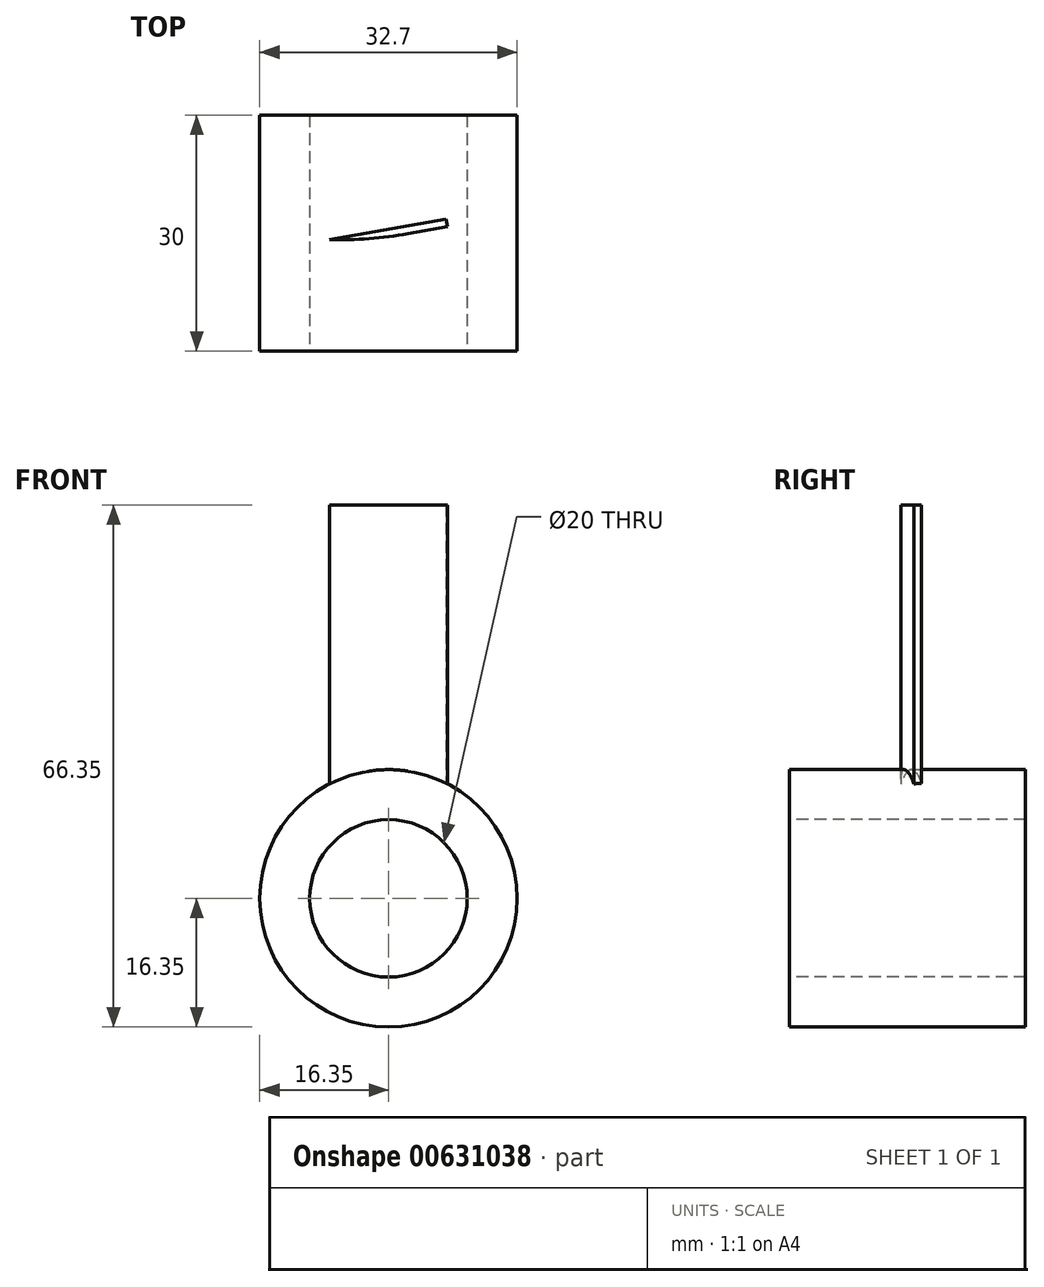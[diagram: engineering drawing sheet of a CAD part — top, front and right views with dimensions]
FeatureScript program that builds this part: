
annotation { "Feature Type Name" : "Feature", "Feature Type Description" : "" }
export const myFeature = defineFeature(function(context is Context, id is Id, definition is map)
    precondition{}
    {
        {
            var Q0;
            Q0=qCreatedBy(makeId("Front.planeOp"),FACE);
            var sketch = newSketch(context, id + "F0", { "sketchPlane" : qUnion([Q0])});
            skCircle(sketch, "E0", {"center": v(0, 0) * mm, "radius": 16.35 * mm});
            skSolve(sketch);
        }
        {
            var Q0;
            Q0 = qSketchRegion(id + "F0", true);
            extrude(context, id + "F1", {"entities" : qUnion([Q0]), "endBound" : BoundingType.SYMMETRIC, "depth" : 30 * mm, "offsetDistance" : 25.4 * mm});
        }
        {
            var Q0;
            Q0=qCreatedBy(makeId("Top.planeOp"),FACE);
            cPlane(context, id + "F2", {"entities" : qUnion([Q0]), "cplaneType" : CPlaneType.OFFSET, "offset" : 10 * mm, "width" : 150 * mm, "height" : 150 * mm});
        }
        {
            var Q0;
            Q0=qCreatedBy(id+"F2.planeOp",FACE);
            var sketch = newSketch(context, id + "F3", { "sketchPlane" : qUnion([Q0])});
            skLineSegment(sketch, "E1.bottom", {"start": v(7.47, 0.8) * mm, "end": v(-7.3, -1.8) * mm});
            skLineSegment(sketch, "E1.top", {"start": v(7.3, 1.8) * mm, "end": v(-7.47, -0.8) * mm});
            skLineSegment(sketch, "E1.left", {"start": v(7.47, 0.8) * mm, "end": v(7.39, 1.3) * mm});
            skLineSegment(sketch, "E1.right", {"start": v(-7.3, -1.8) * mm, "end": v(-7.39, -1.3) * mm});
            skPoint(sketch, "E1.middle", {"position": v(0, 0) * mm});
            skLineSegment(sketch, "E2", {"start": v(-7.39, -1.3) * mm, "end": v(-7.47, -0.8) * mm});
            skLineSegment(sketch, "E3", {"start": v(7.39, 1.3) * mm, "end": v(7.3, 1.8) * mm});
            skLineSegment(sketch, "E4", {"start": v(-7.39, -1.3) * mm, "end": v(0, 0) * mm});
            skLineSegment(sketch, "E5", {"start": v(0, 0) * mm, "end": v(7.39, 1.3) * mm});
            skSolve(sketch);
        }
        {
            var Q0;
            Q0 = qSketchRegion(id + "F3", true);
            extrude(context, id + "F4", {"entities" : qUnion([Q0]), "operationType" : NewBodyOperationType.ADD, "depth" : 40 * mm, "offsetDistance" : 25 * mm});
        }
        {
            var Q0;
            Q0=qCreatedBy(makeId("Top.planeOp"),FACE);
            var sketch = newSketch(context, id + "F5", { "sketchPlane" : qUnion([Q0])});
            skLineSegment(sketch, "E6", {"start": v(0, 34.93) * mm, "end": v(0, -35.3) * mm});
            skSolve(sketch);
        }
        {
            var Q0;
            Q0=makeQuery(id+"F1.opExtrude","CAP_FACE",FACE,{"disambiguationData":[OSD([sQuery(id+"F0.wireOp",EDGE,"E0")])],"isStart":false});
            var sketch = newSketch(context, id + "F6", { "sketchPlane" : qUnion([Q0])});
            skCircle(sketch, "E7", {"center": v(0, 0) * mm, "radius": 10 * mm});
            skSolve(sketch);
        }
        {
            var Q0;
            Q0 = qSketchRegion(id + "F6", true);
            extrude(context, id + "F7", {"entities" : qUnion([Q0]), "operationType" : NewBodyOperationType.REMOVE, "endBound" : BoundingType.THROUGH_ALL, "oppositeDirection" : true, "depth" : 25 * mm, "offsetDistance" : 25 * mm});
        }
        {
            var Q0;
            Q0=makeQuery(id+"F4.opExtrude","SWEPT_EDGE",EDGE,{"disambiguationData":[OSD([sQuery(id+"F3.wireOp",EDGE,"E1.bottom"),sQuery(id+"F3.wireOp",EDGE,"E1.right")])]});
            var Q1;
            Q1=makeQuery(id+"FS7XTIEs3ckikAF_1.1.F4.opExtrude","SWEPT_EDGE",EDGE,{"disambiguationData":[OSD([sQuery(id+"F3.wireOp",EDGE,"E1.bottom"),sQuery(id+"F3.wireOp",EDGE,"E1.right")])]});
            var Q2;
            Q2=makeQuery(id+"FS7XTIEs3ckikAF_1.2.F4.opExtrude","SWEPT_EDGE",EDGE,{"disambiguationData":[OSD([sQuery(id+"F3.wireOp",EDGE,"E1.bottom"),sQuery(id+"F3.wireOp",EDGE,"E1.right")])]});
            fillet(context, id + "F8", {"entities" : qUnion([Q0, Q1, Q2]), "radius" : 50 * mm, "tangentPropagation" : true, "allowEdgeOverflow" : false});
        }
    });
